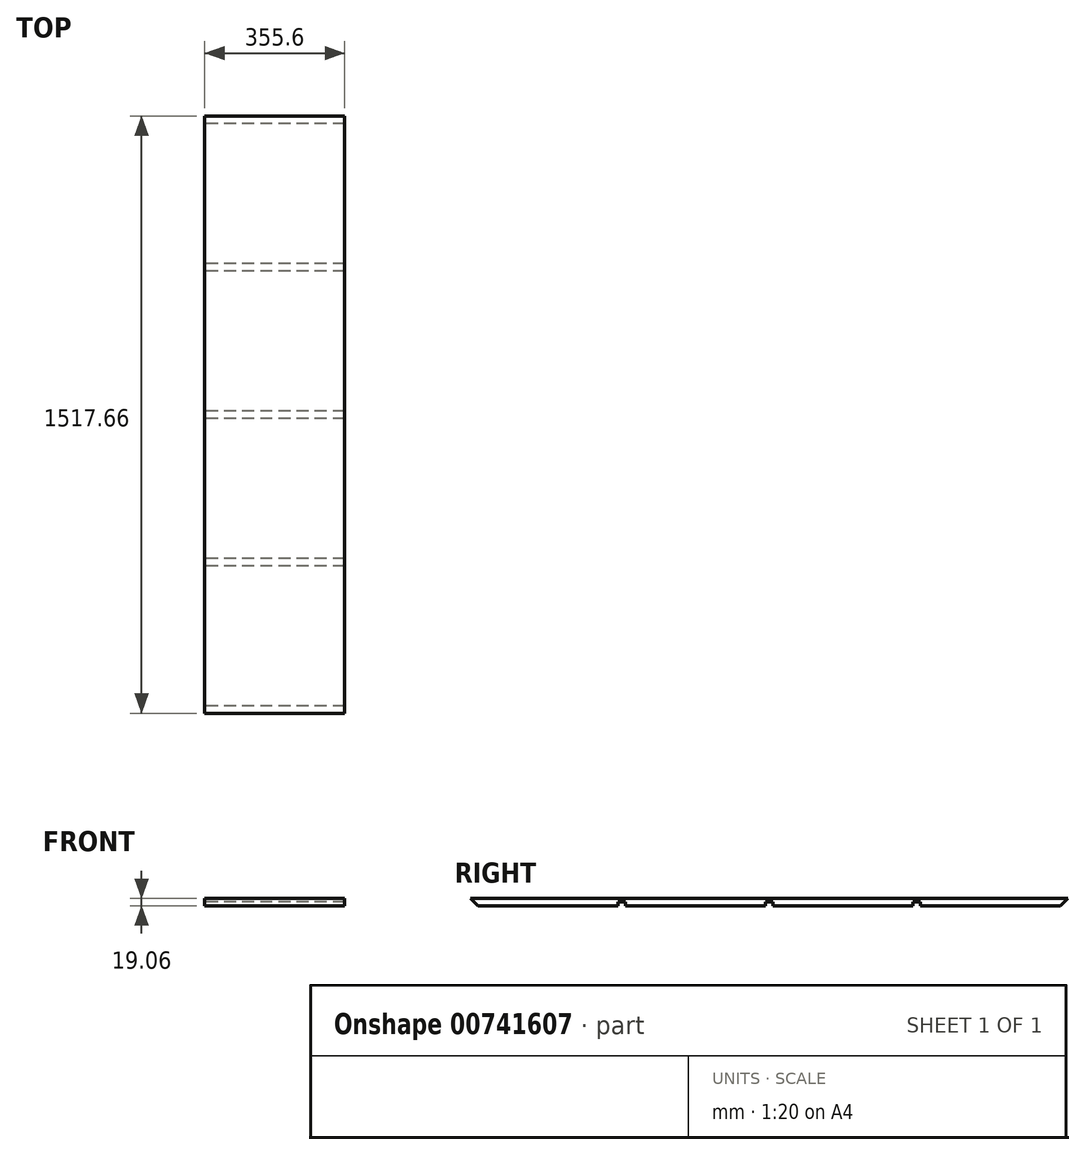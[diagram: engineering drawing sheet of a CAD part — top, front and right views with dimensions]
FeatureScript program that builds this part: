
annotation { "Feature Type Name" : "Feature", "Feature Type Description" : "" }
export const myFeature = defineFeature(function(context is Context, id is Id, definition is map)
    precondition{}
    {
        {
            var Q0;
            Q0=qCreatedBy(makeId("Right.planeOp"),FACE);
            var sketch = newSketch(context, id + "F0", { "sketchPlane" : qUnion([Q0])});
            skLineSegment(sketch, "E0.bottom", {"start": v(758.83, 9.53) * mm, "end": v(-758.83, 9.53) * mm});
            skLineSegment(sketch, "E0.top", {"start": v(739.77, -9.53) * mm, "end": v(384.17, -9.53) * mm});
            skPoint(sketch, "E0.middle", {"position": v(0, 0) * mm});
            skLineSegment(sketch, "E1", {"start": v(-758.83, 9.53) * mm, "end": v(-739.77, -9.53) * mm});
            skPoint(sketch, "E2.orphan", {"position": v(-758.83, -9.53) * mm});
            skLineSegment(sketch, "E3", {"start": v(-739.77, -9.53) * mm, "end": v(-384.17, -9.53) * mm});
            skLineSegment(sketch, "E4.top", {"start": v(-384.17, 0) * mm, "end": v(-365.12, 0) * mm});
            skLineSegment(sketch, "E4.left", {"start": v(-384.17, -9.53) * mm, "end": v(-384.17, 0) * mm});
            skLineSegment(sketch, "E4.right", {"start": v(-365.12, -9.53) * mm, "end": v(-365.12, 0) * mm});
            skLineSegment(sketch, "E5.trimOffspring", {"start": v(-384.17, -9.53) * mm, "end": v(-739.77, -9.53) * mm});
            skLineSegment(sketch, "E6", {"start": v(-365.12, -9.53) * mm, "end": v(-9.52, -9.53) * mm});
            skLineSegment(sketch, "E7.top", {"start": v(-9.52, 0) * mm, "end": v(0, 0) * mm});
            skLineSegment(sketch, "E7.left", {"start": v(-9.52, -9.53) * mm, "end": v(-9.52, 0) * mm});
            skLineSegment(sketch, "E8.trimOffspring", {"start": v(-9.52, -9.53) * mm, "end": v(-365.12, -9.53) * mm});
            skLineSegment(sketch, "E9.MirrorCS", {"start": v(9.52, -9.53) * mm, "end": v(9.52, 0) * mm});
            skLineSegment(sketch, "E10.MirrorCS", {"start": v(9.52, 0) * mm, "end": v(0, 0) * mm});
            skLineSegment(sketch, "E11.MirrorCS", {"start": v(384.17, -9.53) * mm, "end": v(384.17, 0) * mm});
            skLineSegment(sketch, "E12.MirrorCS", {"start": v(384.17, 0) * mm, "end": v(365.12, 0) * mm});
            skLineSegment(sketch, "E13.MirrorCS", {"start": v(365.12, -9.53) * mm, "end": v(365.12, 0) * mm});
            skLineSegment(sketch, "E14.MirrorCS", {"start": v(758.83, 9.53) * mm, "end": v(739.77, -9.53) * mm});
            skLineSegment(sketch, "E15.trimOffspring", {"start": v(365.12, -9.53) * mm, "end": v(9.52, -9.53) * mm});
            skPoint(sketch, "E0.left.end.orphan", {"position": v(758.83, -9.53) * mm});
            skSolve(sketch);
        }
        {
            var Q0;
            Q0 = qSketchRegion(id + "F0", true);
            extrude(context, id + "F1", {"entities" : qUnion([Q0]), "depth" : 355.6 * mm, "offsetDistance" : 25.4 * mm});
        }
    });
